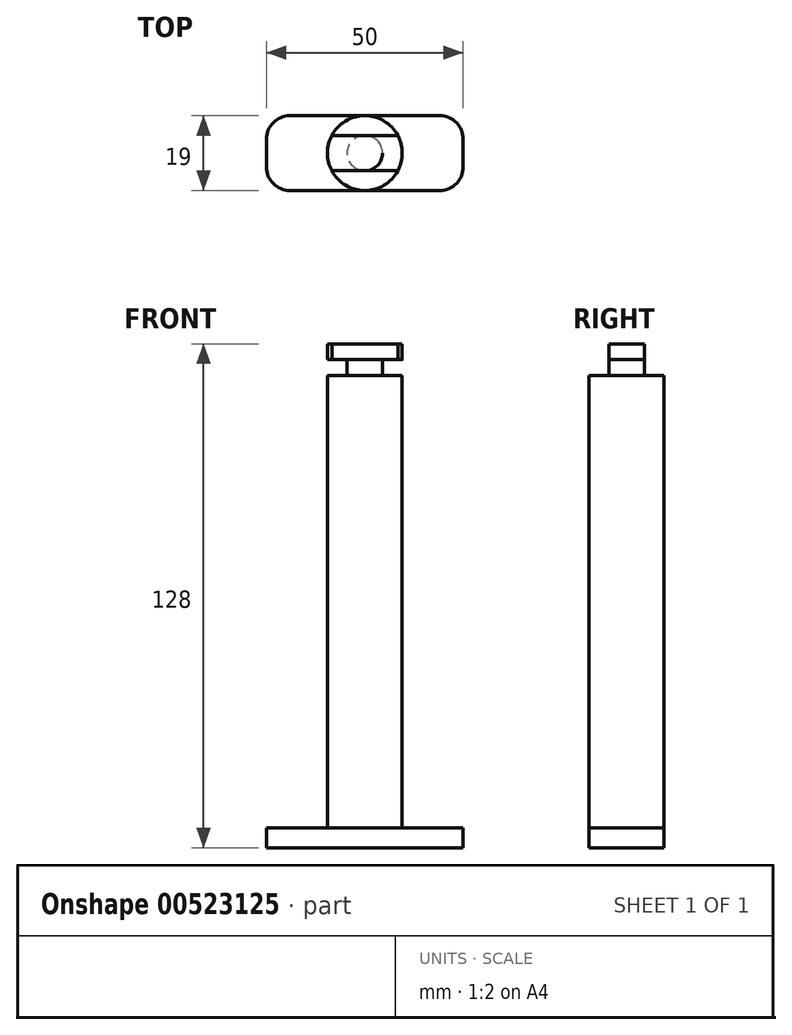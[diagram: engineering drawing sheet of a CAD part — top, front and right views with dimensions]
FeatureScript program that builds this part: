
annotation { "Feature Type Name" : "Feature", "Feature Type Description" : "" }
export const myFeature = defineFeature(function(context is Context, id is Id, definition is map)
    precondition{}
    {
        {
            var Q0;
            Q0=qCreatedBy(makeId("Top.planeOp"),FACE);
            var sketch = newSketch(context, id + "F0", { "sketchPlane" : qUnion([Q0])});
            skCircle(sketch, "E0", {"center": v(0, 0) * mm, "radius": 9.5 * mm});
            skLineSegment(sketch, "E1.bottom", {"start": v(-25, 9.5) * mm, "end": v(25, 9.5) * mm});
            skLineSegment(sketch, "E1.top", {"start": v(-25, -9.5) * mm, "end": v(25, -9.5) * mm});
            skLineSegment(sketch, "E1.left", {"start": v(-25, 9.5) * mm, "end": v(-25, -9.5) * mm});
            skLineSegment(sketch, "E1.right", {"start": v(25, 9.5) * mm, "end": v(25, -9.5) * mm});
            skSolve(sketch);
        }
        {
            var Q0;
            Q0=makeQuery(id+"F0.imprint","IMPRINT",FACE,{"disambiguationData":[TD([[makeQuery(id+"F0.imprint","IMPRINT",EDGE,{"derivedFrom":sQuery(id+"F0.wireOp",EDGE,"E0")}),1.0]])]});
            extrude(context, id + "F1", {"entities" : qUnion([Q0]), "depth" : 115 * mm, "offsetDistance" : 25 * mm});
        }
        {
            var Q0;
            {var subQ5=sQuery(id+"F0.wireOp",EDGE,"E1.left");Q0=makeQuery(id+"F0.imprint","IMPRINT",FACE,{"disambiguationData":[TD([[makeQuery(id+"F0.imprint","IMPRINT",EDGE,{"derivedFrom":subQ5}),1.0]])]});}
            var Q1;
            {var subQ5=sQuery(id+"F0.wireOp",EDGE,"E1.right");Q1=makeQuery(id+"F0.imprint","IMPRINT",FACE,{"disambiguationData":[TD([[makeQuery(id+"F0.imprint","IMPRINT",EDGE,{"derivedFrom":subQ5}),-1.0]])]});}
            var Q2;
            {var subQ0=sQuery(id+"F0.wireOp",EDGE,"E0");var subQ1=makeQuery(id+"F0.imprint","INTERSECT",VERTEX,{"derivedFrom":[subQ0,sQuery(id+"F0.wireOp",EDGE,"E1.bottom")]});Q2=makeQuery(id+"F0.imprint","IMPRINT",FACE,{"disambiguationData":[TD([[makeQuery(id+"F0.imprint","IMPRINT",EDGE,{"disambiguationData":[TD([[subQ1,-1.0]])],"derivedFrom":subQ0}),1.0]])]});}
            extrude(context, id + "F2", {"entities" : qUnion([Q0, Q1, Q2]), "operationType" : NewBodyOperationType.ADD, "oppositeDirection" : true, "depth" : 5 * mm, "offsetDistance" : 25 * mm});
        }
        {
            var Q0;
            Q0=makeQuery(id+"F2.opExtrude","SWEPT_EDGE",EDGE,{"disambiguationData":[OSD([sQuery(id+"F0.wireOp",EDGE,"E1.bottom"),sQuery(id+"F0.wireOp",EDGE,"E1.left")])]});
            var Q1;
            Q1=makeQuery(id+"F2.opExtrude","SWEPT_EDGE",EDGE,{"disambiguationData":[OSD([sQuery(id+"F0.wireOp",EDGE,"E1.top"),sQuery(id+"F0.wireOp",EDGE,"E1.left")])]});
            var Q2;
            Q2=makeQuery(id+"F2.opExtrude","SWEPT_EDGE",EDGE,{"disambiguationData":[OSD([sQuery(id+"F0.wireOp",EDGE,"E1.bottom"),sQuery(id+"F0.wireOp",EDGE,"E1.right")])]});
            var Q3;
            Q3=makeQuery(id+"F2.opExtrude","SWEPT_EDGE",EDGE,{"disambiguationData":[OSD([sQuery(id+"F0.wireOp",EDGE,"E1.top"),sQuery(id+"F0.wireOp",EDGE,"E1.right")])]});
            fillet(context, id + "F3", {"entities" : qUnion([Q0, Q1, Q2, Q3]), "radius" : 6 * mm, "tangentPropagation" : true, "allowEdgeOverflow" : false});
        }
        {
            var Q0;
            Q0=makeQuery(id+"F1.opExtrude","CAP_FACE",FACE,{"disambiguationData":[OSD([sQuery(id+"F0.wireOp",EDGE,"E0")])],"isStart":false});
            var sketch = newSketch(context, id + "F4", { "sketchPlane" : qUnion([Q0])});
            skCircle(sketch, "E2", {"center": v(0, 0) * mm, "radius": 4.5 * mm});
            skSolve(sketch);
        }
        {
            var Q0;
            Q0=makeQuery(id+"F4.imprint","IMPRINT",FACE,{"disambiguationData":[TD([[makeQuery(id+"F4.imprint","IMPRINT",EDGE,{"derivedFrom":sQuery(id+"F4.wireOp",EDGE,"E2")}),1.0]])]});
            extrude(context, id + "F5", {"entities" : qUnion([Q0]), "operationType" : NewBodyOperationType.ADD, "depth" : 4 * mm, "offsetDistance" : 25 * mm});
        }
        {
            var Q0;
            Q0=makeQuery(id+"F5.opExtrude","CAP_FACE",FACE,{"disambiguationData":[OSD([sQuery(id+"F4.wireOp",EDGE,"E2")])],"isStart":false});
            var sketch = newSketch(context, id + "F6", { "sketchPlane" : qUnion([Q0])});
            skLineSegment(sketch, "E3.bottom", {"start": v(-9.5, 4.5) * mm, "end": v(9.5, 4.5) * mm});
            skLineSegment(sketch, "E3.top", {"start": v(-9.5, -4.5) * mm, "end": v(9.5, -4.5) * mm});
            skLineSegment(sketch, "E3.left", {"start": v(-9.5, 4.5) * mm, "end": v(-9.5, -4.5) * mm});
            skLineSegment(sketch, "E3.right", {"start": v(9.5, 4.5) * mm, "end": v(9.5, -4.5) * mm});
            skPoint(sketch, "E3.middle", {"position": v(0, 0) * mm});
            skCircle(sketch, "E4", {"center": v(0, 0) * mm, "radius": 9.5 * mm});
            skSolve(sketch);
        }
        {
            var Q0;
            {var subQ0=makeQuery(id+"F5.opExtrude","CAP_EDGE",EDGE,{"disambiguationData":[OSD([sQuery(id+"F4.wireOp",EDGE,"E2")])],"isStart":false});var subQ1=makeQuery(id+"F6.imprint","INTERSECT",VERTEX,{"derivedFrom":[subQ0,sQuery(id+"F6.wireOp",EDGE,"E3.bottom")]});Q0=makeQuery(id+"F6.imprint","IMPRINT",FACE,{"disambiguationData":[TD([[makeQuery(id+"F6.imprint","IMPRINT",EDGE,{"disambiguationData":[TD([[subQ1,-1.0]])],"derivedFrom":subQ0}),1.0]])]});}
            var Q1;
            {var subQ0=sQuery(id+"F6.wireOp",EDGE,"E4");var subQ1=sQuery(id+"F6.wireOp",EDGE,"E3.bottom");var subQ2=makeQuery(id+"F6.imprint","INTERSECT",VERTEX,{"disambiguationData":[OD(0.0)],"derivedFrom":[subQ1,subQ0]});Q1=makeQuery(id+"F6.imprint","IMPRINT",FACE,{"disambiguationData":[TD([[makeQuery(id+"F6.imprint","IMPRINT",EDGE,{"disambiguationData":[TD([[subQ2,-1.0]])],"derivedFrom":subQ1}),-1.0]])]});}
            var Q2;
            {var subQ0=sQuery(id+"F6.wireOp",EDGE,"E4");var subQ6=sQuery(id+"F6.wireOp",EDGE,"E3.bottom");var subQ7=makeQuery(id+"F6.imprint","INTERSECT",VERTEX,{"disambiguationData":[OD(1.0)],"derivedFrom":[subQ6,subQ0]});Q2=makeQuery(id+"F6.imprint","IMPRINT",FACE,{"disambiguationData":[TD([[makeQuery(id+"F6.imprint","IMPRINT",EDGE,{"disambiguationData":[TD([[subQ7,1.0]])],"derivedFrom":subQ6}),-1.0]])]});}
            extrude(context, id + "F7", {"entities" : qUnion([Q0, Q1, Q2]), "operationType" : NewBodyOperationType.ADD, "depth" : 4 * mm, "offsetDistance" : 25 * mm});
        }
    });
